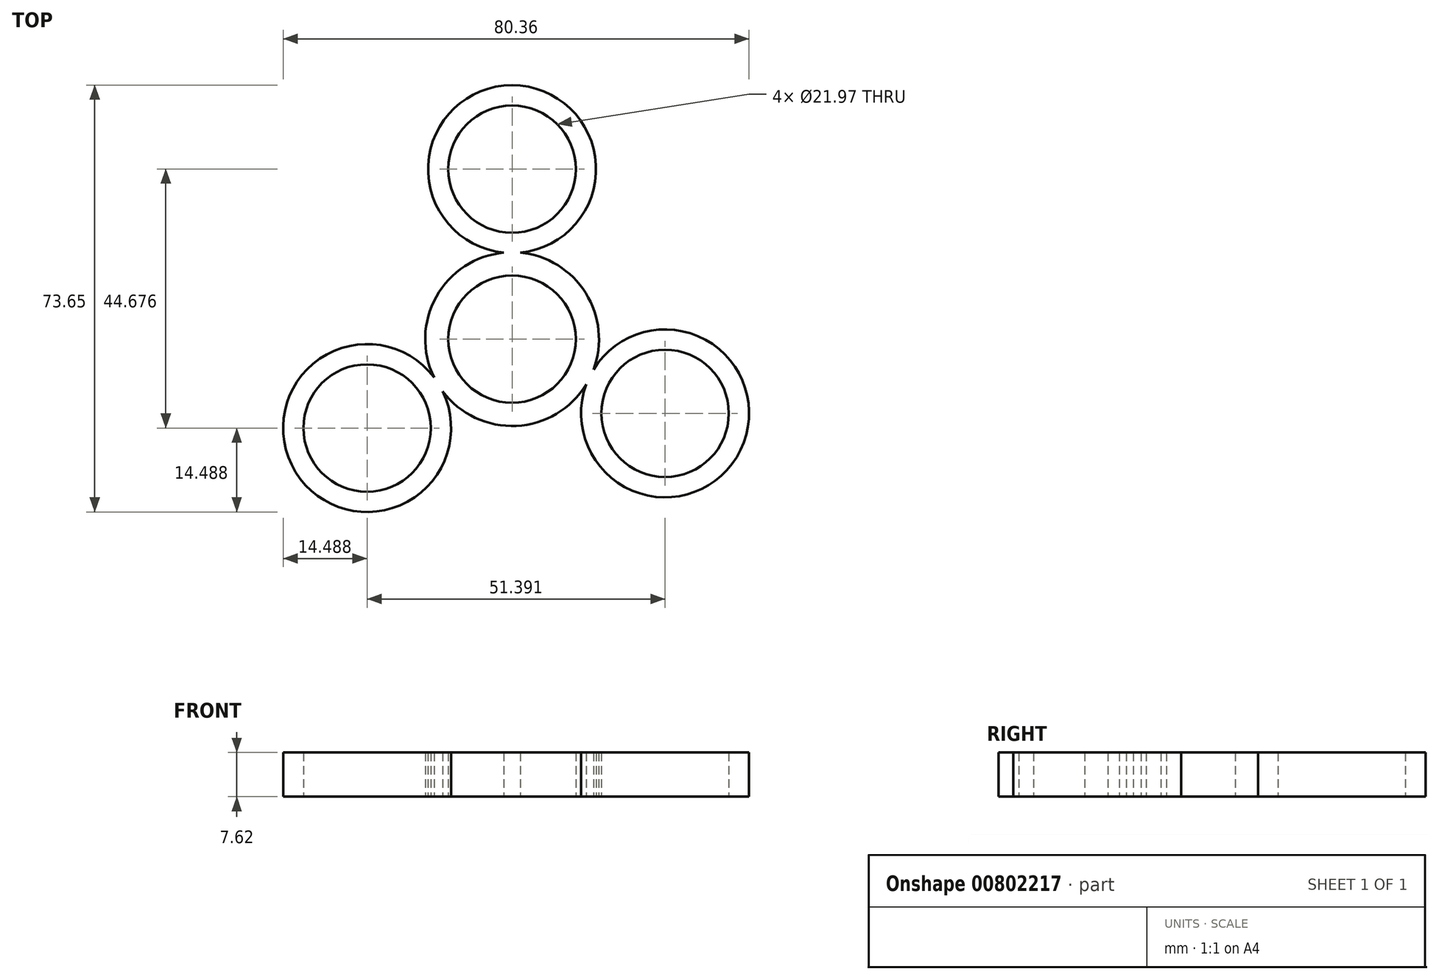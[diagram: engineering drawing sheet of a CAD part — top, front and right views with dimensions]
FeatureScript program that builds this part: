
annotation { "Feature Type Name" : "Feature", "Feature Type Description" : "" }
export const myFeature = defineFeature(function(context is Context, id is Id, definition is map)
    precondition{}
    {
        {
            var Q0;
            Q0=qCreatedBy(makeId("Top.planeOp"),FACE);
            var sketch = newSketch(context, id + "F0", { "sketchPlane" : qUnion([Q0])});
            skCircle(sketch, "E0", {"center": v(0, 0) * mm, "radius": 10.99 * mm});
            skCircle(sketch, "E1", {"center": v(0, 29.33) * mm, "radius": 10.99 * mm});
            skCircle(sketch, "E2", {"center": v(26.39, -12.8) * mm, "radius": 10.99 * mm});
            skCircle(sketch, "E3", {"center": v(-25, -15.34) * mm, "radius": 10.99 * mm});
            skArc(sketch, "E4", {"start": v(1.42, 14.92) * mm, "mid": v(0, 43.82) * mm, "end": v(-1.42, 14.92) * mm});
            skArc(sketch, "E5", {"start": v(-1.42, 14.92) * mm, "mid": v(-13.08, 7.32) * mm, "end": v(-13.46, -6.6) * mm});
            skArc(sketch, "E6", {"start": v(12.8, -7.8) * mm, "mid": v(39.42, -19.14) * mm, "end": v(14.04, -5.24) * mm});
            skArc(sketch, "E7", {"start": v(-13.46, -6.6) * mm, "mid": v(-37.35, -22.92) * mm, "end": v(-11.97, -9.02) * mm});
            skArc(sketch, "E8.trimOffspring", {"start": v(14.04, -5.24) * mm, "mid": v(12.7, 7.95) * mm, "end": v(1.42, 14.92) * mm});
            skArc(sketch, "E9.trimOffspring", {"start": v(-11.97, -9.02) * mm, "mid": v(0.74, -14.97) * mm, "end": v(12.8, -7.8) * mm});
            skArc(sketch, "E10", {"start": v(0, 29.33) * mm, "mid": v(-25.6, 14.33) * mm, "end": v(-25, -15.34) * mm, "construction": true});
            skArc(sketch, "E11", {"start": v(26.39, -12.8) * mm, "mid": v(24.86, 15.57) * mm, "end": v(0, 29.33) * mm, "construction": true});
            skArc(sketch, "E12", {"start": v(-25, -15.34) * mm, "mid": v(1.44, -29.3) * mm, "end": v(26.39, -12.8) * mm, "construction": true});
            skSolve(sketch);
        }
        {
            var Q0;
            Q0=qSketchRegion(id+"F0",true);
            extrude(context, id + "F1", {"entities" : qUnion([Q0]), "depth" : 7.62 * mm, "offsetDistance" : 25.4 * mm});
        }
    });
